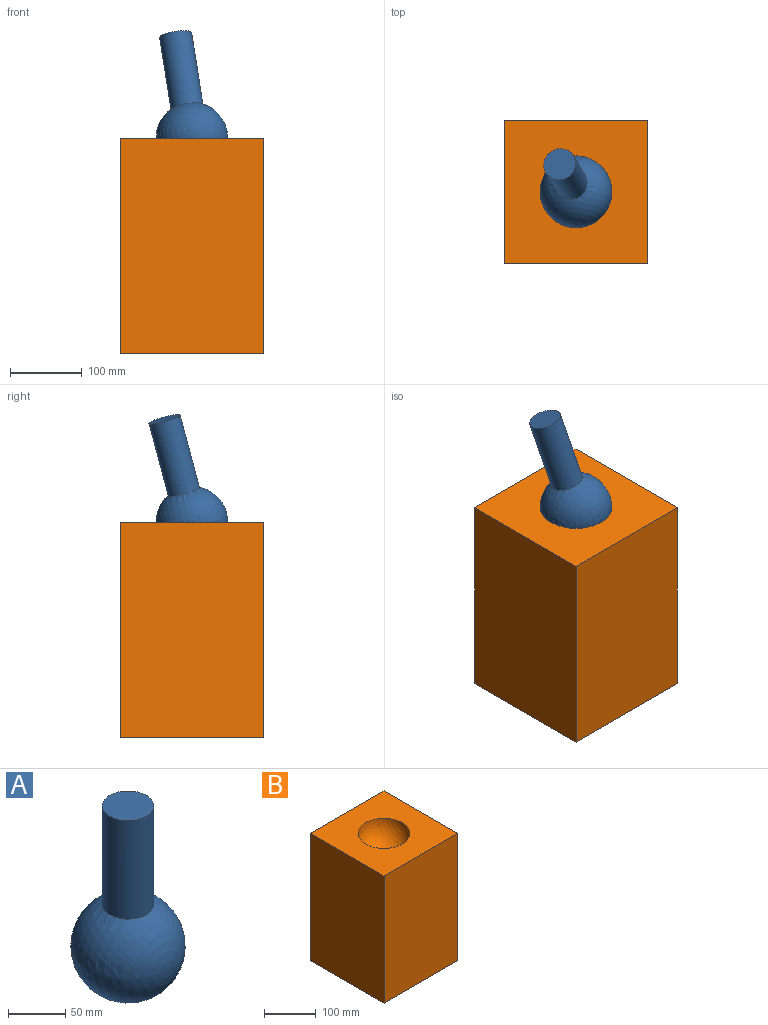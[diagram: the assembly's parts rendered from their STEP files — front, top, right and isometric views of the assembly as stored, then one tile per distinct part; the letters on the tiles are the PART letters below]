
ASSEMBLY  parts=2 mates=1
PART A: 3 faces, bbox 100x100x200 mm
  f0: sphere r=50mm, area 29735.5mm2, adj f1
  f1: cylinder r=22.5mm len=105.35mm, axis (0,0,-1), area 14893.3mm2, adj f0,f2
  f2: plane 45x45mm, normal (0,0,1), area 1590.4mm2, adj f1
PART B: 7 faces, bbox 200x200x300 mm
  f0: plane 300x200mm, normal (0,-1,0), area 60000mm2, adj f1,f3,f4,f5
  f1: plane 300x200mm, normal (1,0,0), area 60000mm2, adj f0,f2,f4,f5
  f2: plane 300x200mm, normal (0,1,0), area 60000mm2, adj f1,f3,f4,f5
  f3: plane 300x200mm, normal (-1,0,0), area 60000mm2, adj f0,f2,f4,f5
  f4: plane 200x200mm, normal (0,0,1), area 32146mm2, adj f0,f1,f2,f3,f6
  f5: plane 200x200mm, normal (0,0,-1), area 40000mm2, adj f0,f1,f2,f3
  f6: sphere r=50mm, area 15708mm2, adj f4
PLACE A rot(axis=(-0.83,-0.53,-0.19),17.6deg) t=(-6.98,8.63,164.85)mm
PLACE B t=(-6.98,8.63,-135.15)mm fixed
MATE ball A.f1 <-> B.f4  axis (-0.15,0.25,0.96) through (-6.98,8.63,164.85)mm
